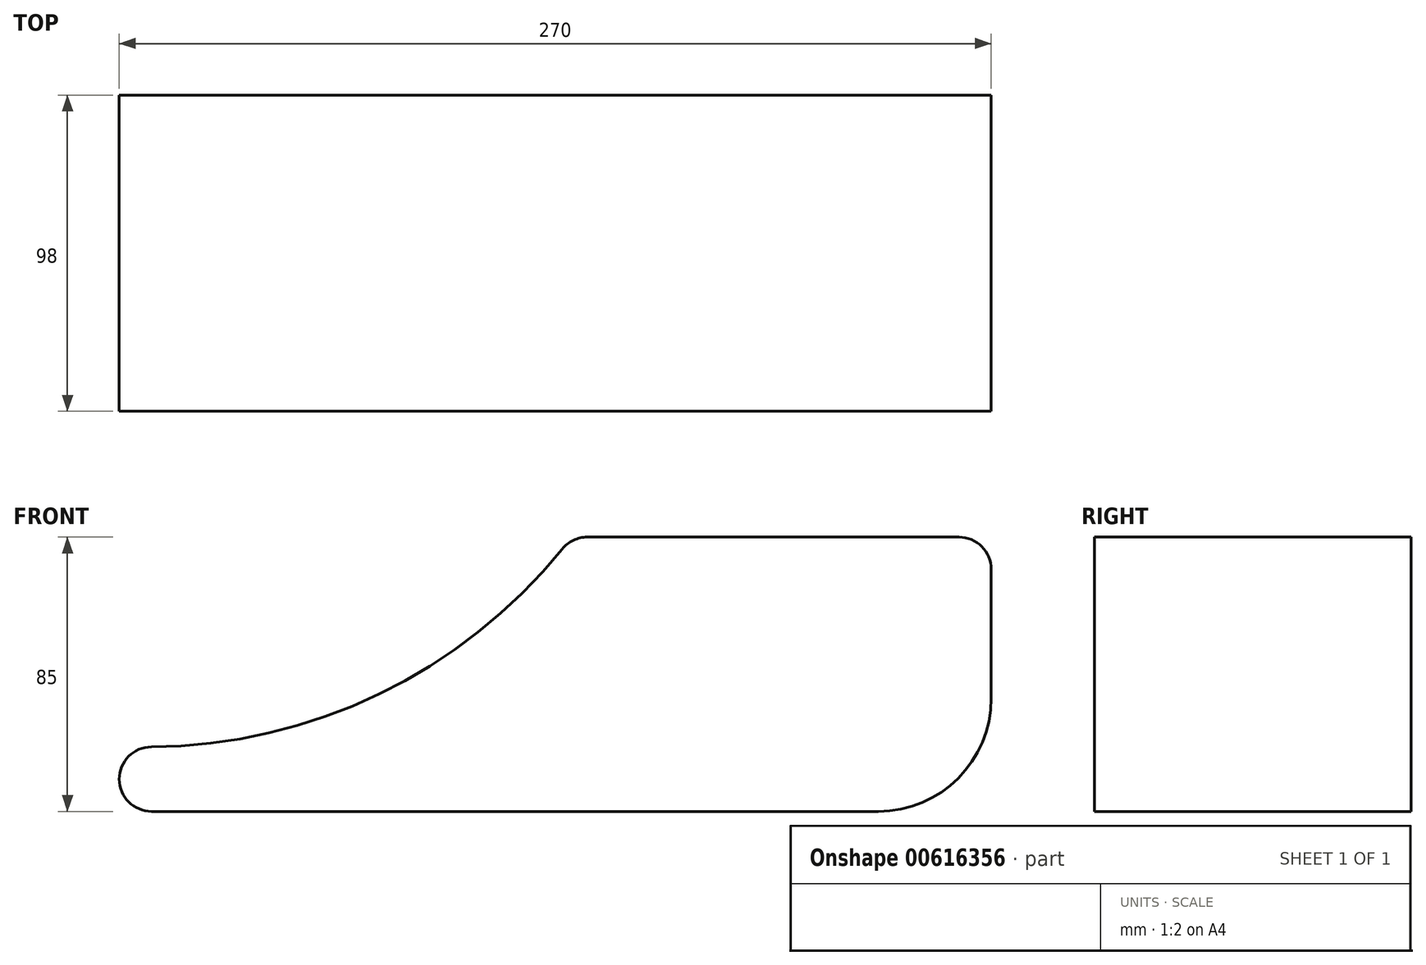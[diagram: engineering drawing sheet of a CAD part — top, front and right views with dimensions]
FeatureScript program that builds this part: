
annotation { "Feature Type Name" : "Feature", "Feature Type Description" : "" }
export const myFeature = defineFeature(function(context is Context, id is Id, definition is map)
    precondition{}
    {
        {
            var Q0;
            Q0=qCreatedBy(makeId("Front.planeOp"),FACE);
            var sketch = newSketch(context, id + "F0", { "sketchPlane" : qUnion([Q0])});
            skLineSegment(sketch, "E0", {"start": v(134.93, 85) * mm, "end": v(250, 85) * mm});
            skLineSegment(sketch, "E1", {"start": v(260, 75) * mm, "end": v(260, 35) * mm});
            skLineSegment(sketch, "E2", {"start": v(225, 0) * mm, "end": v(0, 0) * mm});
            skArc(sketch, "E3", {"start": v(-0.07, 20) * mm, "mid": v(70.43, 36.34) * mm, "end": v(127.16, 81.29) * mm});
            skPoint(sketch, "E4.visualSharp", {"position": v(260, 85) * mm});
            skArc(sketch, "E4.filletArc", {"start": v(260, 75) * mm, "mid": v(257.07, 82.07) * mm, "end": v(250, 85) * mm});
            skArc(sketch, "E5", {"start": v(225, 0) * mm, "mid": v(249.75, 10.25) * mm, "end": v(260, 35) * mm});
            skPoint(sketch, "E6.orphan", {"position": v(260, 0) * mm});
            skArc(sketch, "E7", {"start": v(-0.07, 20) * mm, "mid": v(-10, 9.97) * mm, "end": v(0, 0) * mm});
            skPoint(sketch, "E8.visualSharp", {"position": v(130.07, 85) * mm});
            skArc(sketch, "E8.filletArc", {"start": v(134.93, 85) * mm, "mid": v(130.62, 84.02) * mm, "end": v(127.16, 81.29) * mm});
            skSolve(sketch);
        }
        {
            var Q0;
            Q0 = qSketchRegion(id + "F0", true);
            extrude(context, id + "F1", {"entities" : qUnion([Q0]), "depth" : 98 * mm, "offsetDistance" : 25 * mm});
        }
    });
